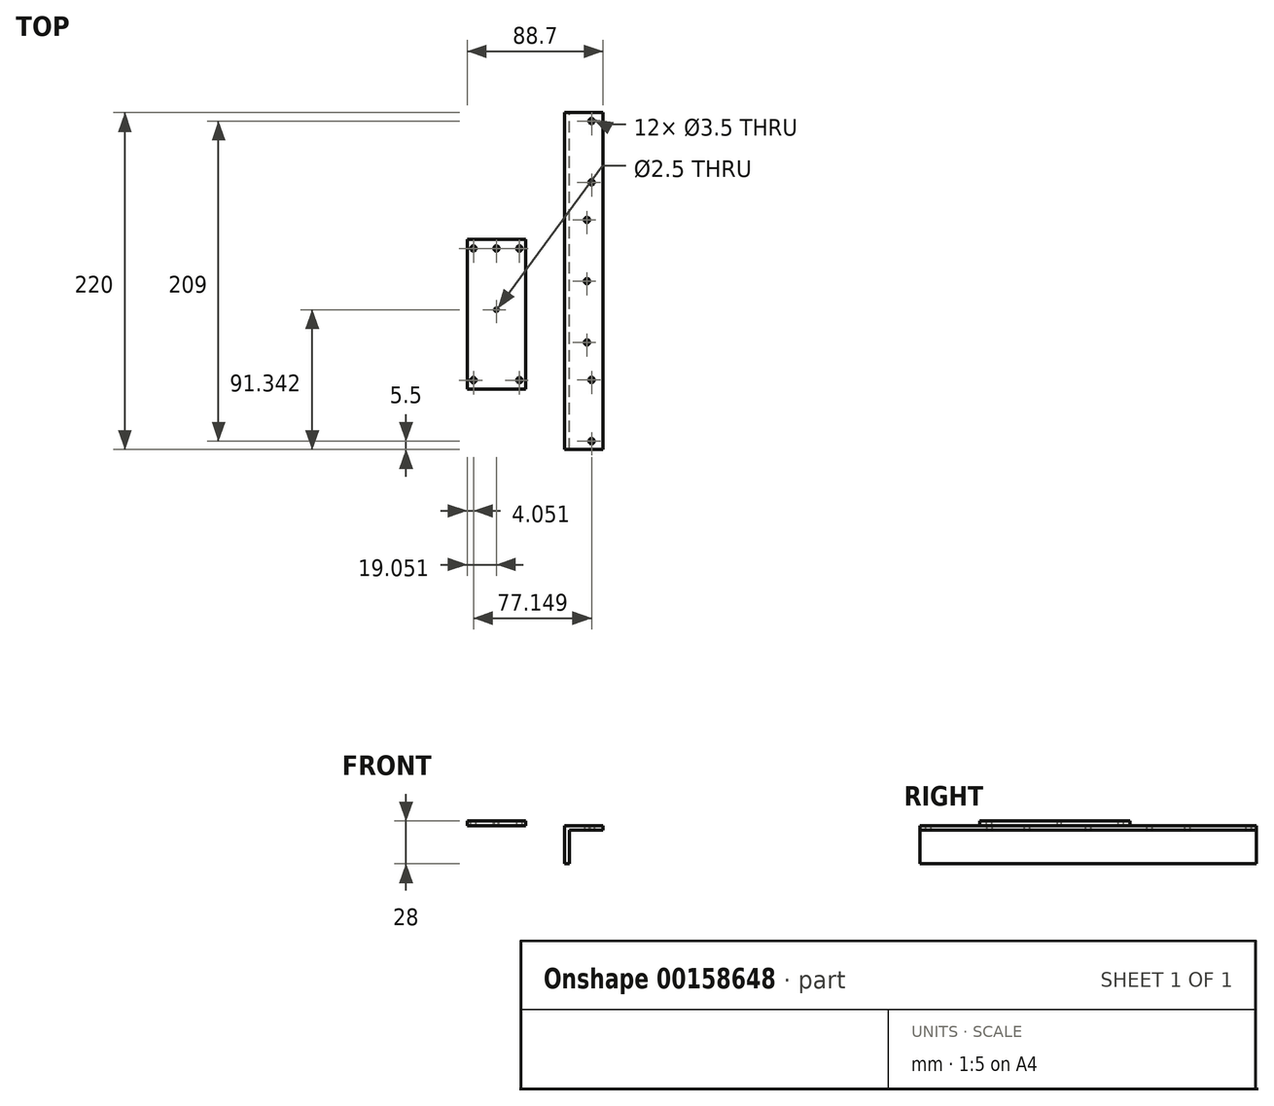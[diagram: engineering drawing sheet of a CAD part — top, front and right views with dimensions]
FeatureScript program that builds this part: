
annotation { "Feature Type Name" : "Feature", "Feature Type Description" : "" }
export const myFeature = defineFeature(function(context is Context, id is Id, definition is map)
    precondition{}
    {
        {
            var Q0;
            Q0=qCreatedBy(makeId("Front.planeOp"),FACE);
            var sketch = newSketch(context, id + "F0", { "sketchPlane" : qUnion([Q0])});
            skLineSegment(sketch, "E0", {"start": v(0, 0) * mm, "end": v(25, 0) * mm});
            skLineSegment(sketch, "E1", {"start": v(25, 0) * mm, "end": v(25, -3) * mm});
            skLineSegment(sketch, "E2", {"start": v(25, -3) * mm, "end": v(3, -3) * mm});
            skLineSegment(sketch, "E3", {"start": v(3, -3) * mm, "end": v(3, -25) * mm});
            skLineSegment(sketch, "E4", {"start": v(3, -25) * mm, "end": v(0, -25) * mm});
            skLineSegment(sketch, "E5", {"start": v(0, -25) * mm, "end": v(0, 0) * mm});
            skSolve(sketch);
        }
        {
            var Q0;
            Q0 = qSketchRegion(id + "F0", true);
            extrude(context, id + "F1", {"entities" : qUnion([Q0]), "endBound" : BoundingType.SYMMETRIC, "depth" : 220 * mm});
        }
        {
            var Q0;
            Q0=makeQuery(id+"F1.opExtrude","SWEPT_FACE",FACE,{"disambiguationData":[OSD([sQuery(id+"F0.wireOp",EDGE,"E2")])]});
            var sketch = newSketch(context, id + "F2", { "sketchPlane" : qUnion([Q0])});
            skLineSegment(sketch, "E6", {"start": v(17.5, 110) * mm, "end": v(17.5, -110) * mm, "construction": true});
            skCircle(sketch, "E7", {"center": v(17.5, 104.5) * mm, "radius": 1.75 * mm});
            skCircle(sketch, "E8", {"center": v(17.5, -104.5) * mm, "radius": 1.75 * mm});
            skCircle(sketch, "E9", {"center": v(17.5, 64.5) * mm, "radius": 1.75 * mm});
            skCircle(sketch, "E10", {"center": v(17.5, -64.5) * mm, "radius": 1.75 * mm});
            skSolve(sketch);
        }
        {
            var Q0;
            Q0 = qSketchRegion(id + "F2", true);
            extrude(context, id + "F3", {"entities" : qUnion([Q0]), "operationType" : NewBodyOperationType.REMOVE, "endBound" : BoundingType.THROUGH_ALL, "oppositeDirection" : true, "depth" : 25 * mm});
        }
        {
            var Q0;
            Q0=qCreatedBy(makeId("Top.planeOp"),FACE);
            var sketch = newSketch(context, id + "F4", { "sketchPlane" : qUnion([Q0])});
            skLineSegment(sketch, "E11.bottom", {"start": v(-63.7, 27.34) * mm, "end": v(-25.6, 27.34) * mm});
            skLineSegment(sketch, "E11.top", {"start": v(-63.7, -70.66) * mm, "end": v(-25.6, -70.66) * mm});
            skLineSegment(sketch, "E11.left", {"start": v(-63.7, 27.34) * mm, "end": v(-63.7, -70.66) * mm});
            skLineSegment(sketch, "E11.right", {"start": v(-25.6, 27.34) * mm, "end": v(-25.6, -70.66) * mm});
            skSolve(sketch);
        }
        {
            var Q0;
            Q0 = qSketchRegion(id + "F4", true);
            extrude(context, id + "F5", {"entities" : qUnion([Q0]), "depth" : 3 * mm});
        }
        {
            var Q0;
            Q0=makeQuery(id+"F1.opExtrude","SWEPT_FACE",FACE,{"disambiguationData":[OSD([sQuery(id+"F0.wireOp",EDGE,"E2")])]});
            var sketch = newSketch(context, id + "F6", { "sketchPlane" : qUnion([Q0])});
            skLineSegment(sketch, "E12", {"start": v(14.5, 40) * mm, "end": v(14.5, -40) * mm, "construction": true});
            skCircle(sketch, "E13", {"center": v(14.5, 40) * mm, "radius": 1.75 * mm});
            skCircle(sketch, "E14", {"center": v(14.5, 0) * mm, "radius": 1.75 * mm});
            skCircle(sketch, "E15", {"center": v(14.5, -40) * mm, "radius": 1.75 * mm});
            skSolve(sketch);
        }
        {
            var Q0;
            Q0 = qSketchRegion(id + "F6", true);
            extrude(context, id + "F7", {"entities" : qUnion([Q0]), "operationType" : NewBodyOperationType.REMOVE, "endBound" : BoundingType.THROUGH_ALL, "oppositeDirection" : true, "depth" : 25 * mm});
        }
        {
            var Q0;
            Q0=makeQuery(id+"F5.opExtrude","CAP_FACE",FACE,{"disambiguationData":[OSD([sQuery(id+"F4.wireOp",EDGE,"E11.bottom"),sQuery(id+"F4.wireOp",EDGE,"E11.top"),sQuery(id+"F4.wireOp",EDGE,"E11.left"),sQuery(id+"F4.wireOp",EDGE,"E11.right")])],"isStart":false});
            var sketch = newSketch(context, id + "F8", { "sketchPlane" : qUnion([Q0])});
            skLineSegment(sketch, "E16.bottom", {"start": v(-59.65, 21.34) * mm, "end": v(-29.65, 21.34) * mm, "construction": true});
            skLineSegment(sketch, "E16.top", {"start": v(-59.65, -64.66) * mm, "end": v(-29.65, -64.66) * mm, "construction": true});
            skLineSegment(sketch, "E16.left", {"start": v(-59.65, 21.34) * mm, "end": v(-59.65, -64.66) * mm, "construction": true});
            skLineSegment(sketch, "E16.right", {"start": v(-29.65, 21.34) * mm, "end": v(-29.65, -64.66) * mm, "construction": true});
            skLineSegment(sketch, "E17", {"start": v(-44.65, -64.66) * mm, "end": v(-44.65, -70.66) * mm, "construction": true});
            skCircle(sketch, "E18", {"center": v(-59.65, 21.34) * mm, "radius": 1.75 * mm});
            skCircle(sketch, "E19", {"center": v(-29.65, 21.34) * mm, "radius": 1.75 * mm});
            skCircle(sketch, "E20", {"center": v(-59.65, -64.66) * mm, "radius": 1.75 * mm});
            skCircle(sketch, "E21", {"center": v(-29.65, -64.66) * mm, "radius": 1.75 * mm});
            skCircle(sketch, "E22", {"center": v(-44.65, 21.34) * mm, "radius": 1.75 * mm});
            skCircle(sketch, "E23", {"center": v(-44.65, -18.66) * mm, "radius": 1.25 * mm});
            skSolve(sketch);
        }
        {
            var Q0;
            Q0 = qSketchRegion(id + "F8", true);
            extrude(context, id + "F9", {"entities" : qUnion([Q0]), "operationType" : NewBodyOperationType.REMOVE, "endBound" : BoundingType.THROUGH_ALL, "oppositeDirection" : true, "depth" : 25 * mm});
        }
    });
